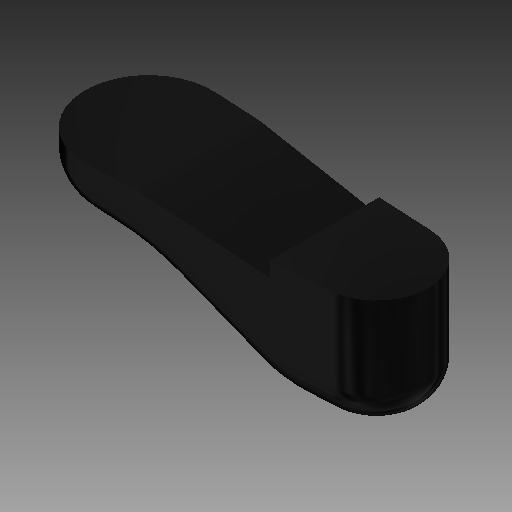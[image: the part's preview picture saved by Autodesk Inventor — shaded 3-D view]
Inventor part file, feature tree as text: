
AUTODESK INVENTOR PART (.ipt)
format: ipt  version: 2022 (Build 260153000, 153)  size: 228,352 bytes
history: native  units: mm (DEFAULTED — no unit token found)
features: extrude x2, fillet x2, sketch x2, other x1
ambient origin geometry x8: Origin, YZ Plane, XZ Plane, XY Plane, X Axis, Y Axis, Z Axis, Center Point
bodies: Solid1 (feature_tree)
feature tree (7):
  other  "iMan - 2D BODY"
  extrude  "Extrusion1"  Depth=10.0mm
  extrude  "Extrusion2"  Depth=27.6606mm
  fillet  "Fillet2"  Radius=138.303mm
  fillet  "Fillet3"  [1 undecoded]
  sketch  "Sketch3"  dims[d1=10.0mm d34=276.606mm]
  sketch  "Sketch4"  dims[d35=83.312mm d36=102.4128mm d38=138.303mm d39=0.0mm d40=83.312mm d43=27.6606mm d44=0.0mm d45=138.303mm d46=27.6606mm d52=94.04604mm d53=35.95878mm d54=4.363323mm d56=1.22173mm d57=91.27998mm d59=82.9818mm d60=12.7mm]
note: 1 required parameter value undecoded (feature->parameter linkage not recoverable at this tier; creation-order binding heuristic only, values carry confidence <= 0.55)
